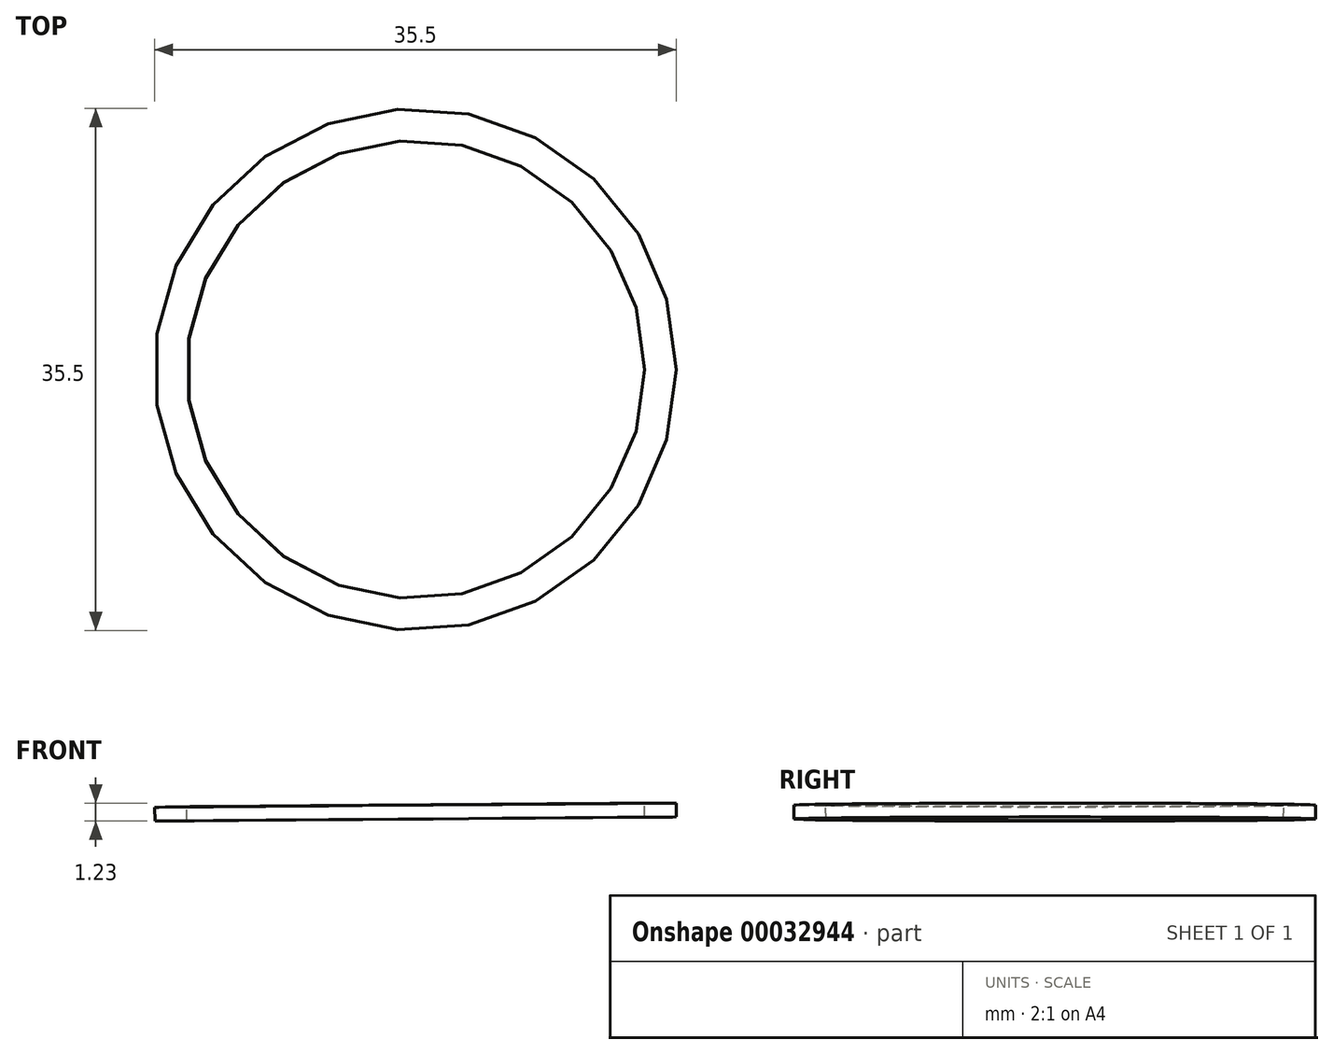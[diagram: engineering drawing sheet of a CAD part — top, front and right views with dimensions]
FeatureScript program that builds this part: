
annotation { "Feature Type Name" : "Feature", "Feature Type Description" : "" }
export const myFeature = defineFeature(function(context is Context, id is Id, definition is map)
    precondition{}
    {
        {
            var Q0;
            Q0=qCreatedBy(makeId("Front.planeOp"),FACE);
            var sketch = newSketch(context, id + "F0", { "sketchPlane" : qUnion([Q0])});
            skLineSegment(sketch, "E0", {"start": v(30.5, 4.18) * mm, "end": v(30.5, 90) * mm});
            skLineSegment(sketch, "E1", {"start": v(13.7, 150) * mm, "end": v(13.7, 171.4) * mm});
            skFitSpline(sketch, "E2", {"points": [v(30.5, 90) * mm, v(19.78, 120) * mm, v(13.7, 150) * mm], "startDerivative": vector(0, 46) * mm, "endDerivative": vector(-0.58, 66.92) * mm});
            skPoint(sketch, "E3.end.orphan", {"position": v(0, 8) * mm});
            skFitSpline(sketch, "E4", {"points": [v(30.5, 0) * mm, v(17.32, 4.54) * mm, v(0, 8) * mm], "startDerivative": vector(-28.51, 9.36) * mm, "endDerivative": vector(-35.1, -0.28) * mm});
            skArc(sketch, "E5.filletArc", {"start": v(26.52, 1.35) * mm, "mid": v(29.24, 1.74) * mm, "end": v(30.5, 4.18) * mm});
            skLineSegment(sketch, "E6.0", {"start": v(14.45, 150) * mm, "end": v(14.45, 171.4) * mm});
            skFitSpline(sketch, "E6.1", {"points": [v(31.25, 90) * mm, v(31.25, 91.01) * mm, v(31.04, 93.14) * mm, v(29.95, 97.74) * mm, v(27.6, 104.06) * mm, v(24.01, 112.1) * mm, v(20.46, 120.07) * mm, v(17.76, 127.47) * mm, v(15.24, 137.06) * mm, v(14.5, 144.47) * mm, v(14.45, 150) * mm]});
            skLineSegment(sketch, "E6.2", {"start": v(31.25, 4.18) * mm, "end": v(31.25, 90) * mm});
            skArc(sketch, "E6.3", {"start": v(26.27, 0.64) * mm, "mid": v(29.67, 1.13) * mm, "end": v(31.25, 4.18) * mm});
            skFitSpline(sketch, "E6.4", {"points": [v(30.27, -0.71) * mm, v(29.07, -0.32) * mm, v(26.74, 0.47) * mm, v(23.32, 1.68) * mm, v(20.43, 2.7) * mm, v(18.05, 3.5) * mm, v(15.6, 4.33) * mm, v(12.41, 5.34) * mm, v(7.07, 6.71) * mm, v(2.86, 7.27) * mm, v(0, 7.25) * mm]});
            skLineSegment(sketch, "E7", {"start": v(14.45, 171.4) * mm, "end": v(13.7, 171.4) * mm});
            skLineSegment(sketch, "E8", {"start": v(0, 44.13) * mm, "end": v(0, 101.73) * mm, "construction": true});
            skLineSegment(sketch, "E9", {"start": v(0, 8) * mm, "end": v(0, 7.25) * mm});
            skLineSegment(sketch, "E10", {"start": v(-21.38, 147) * mm, "end": v(131.81, 147) * mm, "construction": true});
            skLineSegment(sketch, "E11", {"start": v(14.45, 150) * mm, "end": v(16.62, 150) * mm});
            skLineSegment(sketch, "E12", {"start": v(16.62, 150) * mm, "end": v(16.62, 150.95) * mm});
            skLineSegment(sketch, "E13", {"start": v(16.62, 150.95) * mm, "end": v(14.45, 150.95) * mm});
            skSolve(sketch);
        }
        {
            var Q0;
            Q0 = qSketchRegion(id + "F0", true);
            var Q1;
            Q1=sQuery(id+"F0.wireOp",EDGE,"E9");
            revolve(context, id + "F1", {"entities" : qUnion([Q0]), "axis" : qUnion([Q1]), "revolveType" : RevolveType.FULL});
        }
    });
